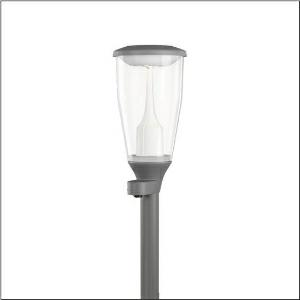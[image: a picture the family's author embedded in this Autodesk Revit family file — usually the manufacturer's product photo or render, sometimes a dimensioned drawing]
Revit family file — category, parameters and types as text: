
# Revit family: dl_11_iq___st1_2a_5xa5575eu14h000022_29dc
name_source: partatom
category: Lighting Fixtures
units: mm (PartAtom-declared; Revit-internal decimal feet)

## family parameters
Cut with Voids When Loaded = No
Host = Face
Light Source = No
Part Type = Normal
Room Calculation Point = No
Round Connector Dimension = Use Diameter
Shared = No

## types (1)
- --- (1 x LED, 1560 lm, 10.7 W, 3000K)
    Apparent Load = 11 VA
    CIE Flux Codes = 24 63 94 96 100
    Color Rendering = 70
    Color Temperature = 3000K
    Default Elevation = 1800 mm
    Description = DL 11 iQ, mast luminaire, Module 540 iQ-SR, primary light control with 3 zone facetted reflector, of plastic, silver coated, highly specular, structured, primary optical cover: cover, of PMMA, transparent, light distribution: ST1.2a, light emission: direct distribution, primary light characteristic: asymmetric, installation type: post-top, LED, High Power LED, rated luminous flux: 1.560lm, luminous efficacy: 146lm/W, light colour: 730, colour temperature: 3000K, control gear: iQ-Street Remote, D4i with power reduction, control: pre-setting: logarithmic dimming characteristic, Street-Remote, Auto-Match, Temp-Guard, Lumen-Switch, Night-Set, Smart-Wire, Light-Fading, Desk-Remote (wireless, voltage-free reading and setting of iQ features in the workshop via application-optimized NFC function/RFID function), optimised constant luminous flux control (CLO 2.0), mains connection: 220..240V, AC, 50/60Hz, connection cable pre-assembled, cable length: 5,5m, start of lifetime: 11W, end of service life: 11W, reduction: 6W, luminaire housing, upper part, of diecast aluminium, coated, Siteco® metallic grey (DB 702S), spigot size: 76mm (post-top), mounting height: 3..5m, post-top mast mounting element, of diecast aluminium, coated, Siteco® metallic grey (DB 702S), Module 540 iQ-SR, traffic white (RAL 9016), equipment: standard, Smart Interface below, protection rating (complete): IP66, insulation class (complete): insulation class II (safety insulation), certification: CE, ENEC, ENEC+, VDE, impact resistance: IK07, packaging unit: 1 piece

Light Distribution: ST1.2a
    Height = 665 mm
    Lamp = 1 x LED
    Lamp Light Flux = 1560 lm
    Lamp Power = 10.7 W
    Lamp count = 1
    Length = 334 mm
    Luminous efficacy = 146 lm/W
    Manufacturer = Siteco
    ModVariant = No
    Model = 5XA5575EU14H000022
    Number of Poles = 1
    OnlyDefault = Yes
    Power Factor = 1
    Product Name = DL 11 iQ | ST1.2a
    Product group = mast luminaire | pylon top
    ProductGroupID = 6100
    Protection Class = Protection class II
    Protection Degree = IP 66
    RLX_Detail_Level = 1
    RLX_Emergency_Light_Flux = 0 lm
    RLX_Emergency_Type = 0
    RLX_Emergency_Type_DB = No
    RlxData = <blob elided: 158701 chars, md5=155e4312>
    Socket = socket
    Standby Power = 0 W
    System Light Flux = 1560 lm
    System Power = 11 W
    Type Comments = factory setting: luminous flux: 100 % | dim-lin: 254 | 419 mA
    Type Image = l_1337539.jpg
    URL = http://relux.com
    VarID = @adj_094796
    Voltage = 0 V
    Weight = 0.00 kg
    Width = 0 mm  [stored 0 ft]

note: [stored X ft] marks values corroborated as IEEE doubles in the binary element streams (Revit-internal decimal feet)

## geometry (parser evidence)
native form markers: Blend x4, Sweep x11
no freeform markers — native parametric forms only
